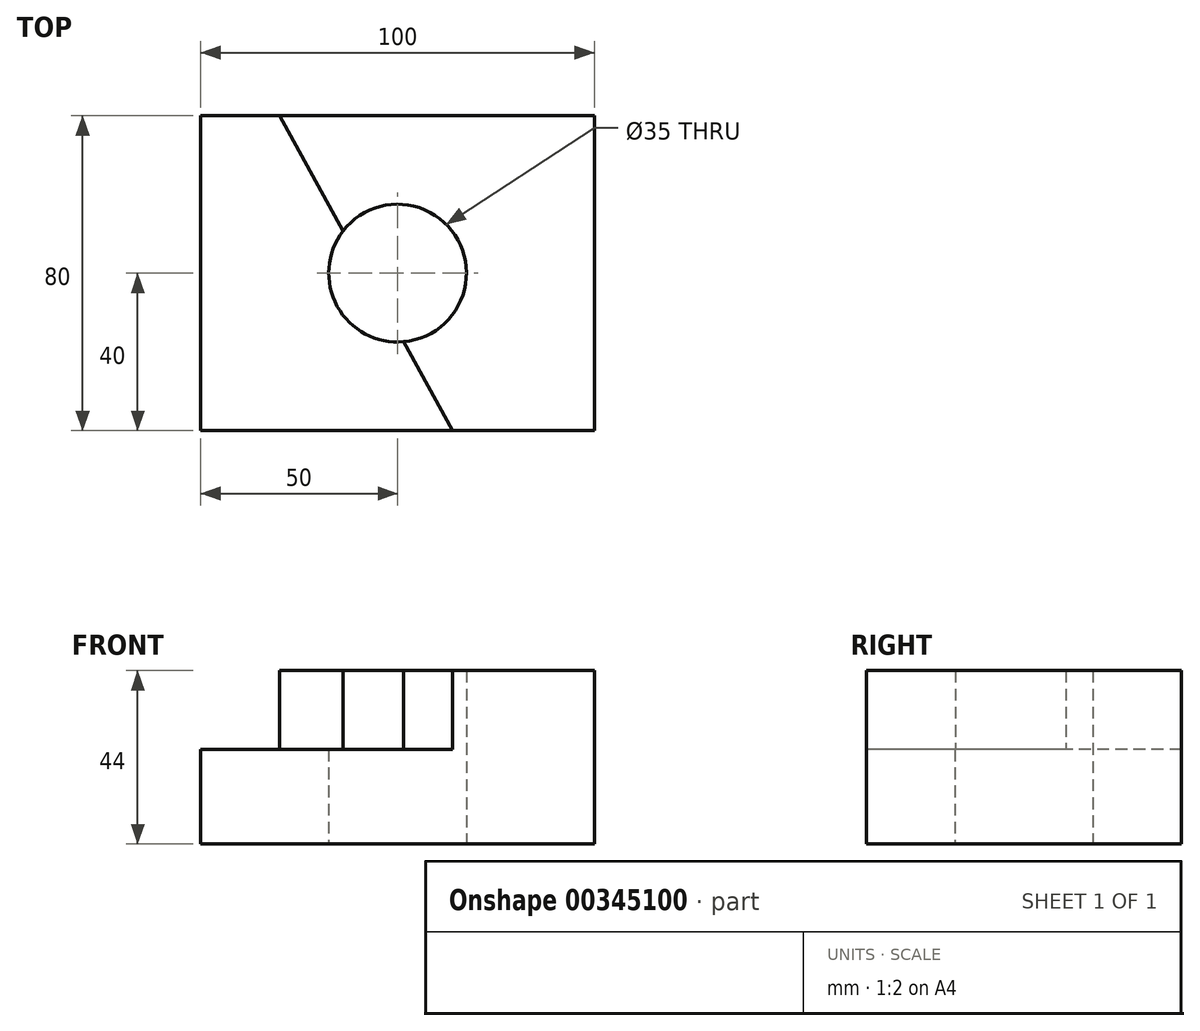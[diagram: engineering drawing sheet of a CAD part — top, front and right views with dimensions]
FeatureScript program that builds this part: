
annotation { "Feature Type Name" : "Feature", "Feature Type Description" : "" }
export const myFeature = defineFeature(function(context is Context, id is Id, definition is map)
    precondition{}
    {
        {
            var Q0;
            Q0=qCreatedBy(makeId("Top.planeOp"),FACE);
            var sketch = newSketch(context, id + "F0", { "sketchPlane" : qUnion([Q0])});
            skLineSegment(sketch, "E0.bottom", {"start": v(50, 40) * mm, "end": v(-50, 40) * mm});
            skLineSegment(sketch, "E0.top", {"start": v(50, -40) * mm, "end": v(-50, -40) * mm});
            skLineSegment(sketch, "E0.left", {"start": v(50, 40) * mm, "end": v(50, -40) * mm});
            skLineSegment(sketch, "E0.right", {"start": v(-50, 40) * mm, "end": v(-50, -40) * mm});
            skPoint(sketch, "E0.middle", {"position": v(0, 0) * mm});
            skCircle(sketch, "E1", {"center": v(0, 0) * mm, "radius": 17.5 * mm});
            skPoint(sketch, "E2", {"position": v(-14, 40) * mm});
            skPoint(sketch, "E3", {"position": v(30, -40) * mm});
            skLineSegment(sketch, "E4", {"start": v(-14, 40) * mm, "end": v(30, -40) * mm});
            skSolve(sketch);
        }
        {
            var Q0;
            {var subQ0=sQuery(id+"F0.wireOp",EDGE,"E0.right");Q0=makeQuery(id+"F0.imprint","IMPRINT",FACE,{"disambiguationData":[TD([[makeQuery(id+"F0.imprint","IMPRINT",EDGE,{"derivedFrom":subQ0}),1.0]])]});}
            var Q1;
            {var subQ0=sQuery(id+"F0.wireOp",EDGE,"E0.left");Q1=makeQuery(id+"F0.imprint","IMPRINT",FACE,{"disambiguationData":[TD([[makeQuery(id+"F0.imprint","IMPRINT",EDGE,{"derivedFrom":subQ0}),-1.0]])]});}
            extrude(context, id + "F1", {"entities" : qUnion([Q0, Q1]), "depth" : 24 * mm});
        }
        {
            var Q0;
            Q0=makeQuery(id+"F1.opExtrude","CAP_FACE",FACE,{"disambiguationData":[OSD([sQuery(id+"F0.wireOp",EDGE,"E0.bottom"),sQuery(id+"F0.wireOp",EDGE,"E0.top"),sQuery(id+"F0.wireOp",EDGE,"E0.left"),sQuery(id+"F0.wireOp",EDGE,"E0.right"),sQuery(id+"F0.wireOp",EDGE,"E1")])],"isStart":false});
            var sketch = newSketch(context, id + "F2", { "sketchPlane" : qUnion([Q0])});
            skPoint(sketch, "E5", {"position": v(50, -40) * mm});
            skPoint(sketch, "E6", {"position": v(14, -40) * mm});
            skPoint(sketch, "E7", {"position": v(50, 40) * mm});
            skPoint(sketch, "E8", {"position": v(-30, 40) * mm});
            skLineSegment(sketch, "E9", {"start": v(-30, 40) * mm, "end": v(-13.87, 10.67) * mm});
            skPoint(sketch, "E10", {"position": v(-13.87, 10.67) * mm});
            skPoint(sketch, "E11", {"position": v(1.59, -17.43) * mm});
            skLineSegment(sketch, "E12.trimOffspring", {"start": v(1.59, -17.43) * mm, "end": v(14, -40) * mm});
            skSolve(sketch);
        }
        {
            var Q0;
            {var subQ2=sQuery(id+"F2.wireOp",EDGE,"E9");Q0=makeQuery(id+"F2.imprint","IMPRINT",FACE,{"disambiguationData":[TD([[makeQuery(id+"F2.imprint","IMPRINT",EDGE,{"derivedFrom":subQ2}),1.0]])]});}
            extrude(context, id + "F3", {"entities" : qUnion([Q0]), "operationType" : NewBodyOperationType.ADD, "depth" : 20 * mm});
        }
    });
